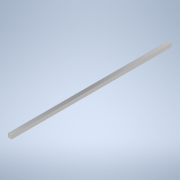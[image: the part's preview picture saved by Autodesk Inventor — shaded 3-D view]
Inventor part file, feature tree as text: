
AUTODESK INVENTOR PART (.ipt)
format: ipt  version: 2020.3 (Build 243373000, 373)  size: 178,688 bytes
history: native  units: mm
features: sketch x8, hole x7, other x1, extrude x1
ambient origin geometry x8: Origin, YZ Plane, XZ Plane, XY Plane, X Axis, Y Axis, Z Axis, Center Point
bodies: Body1 (feature_tree)
feature tree (17):
  other  "ソリッド1"
  extrude  "押し出し1"  Depth=15.0mm
  hole  "穴1"  [1 undecoded]
  hole  "穴2"  [1 undecoded]
  hole  "穴3"  [1 undecoded]
  hole  "穴4"  [1 undecoded]
  hole  "穴5"  [1 undecoded]
  hole  "穴6"  [1 undecoded]
  hole  "穴7"  [1 undecoded]
  sketch  "スケッチ1"
  sketch  "スケッチ2"
  sketch  "スケッチ3"
  sketch  "スケッチ4"
  sketch  "スケッチ6"
  sketch  "スケッチ7"
  sketch  "スケッチ8"
  sketch  "スケッチ9"
note: 7 required parameter values undecoded (feature->parameter linkage not recoverable at this tier; creation-order binding heuristic only, values carry confidence <= 0.55)
